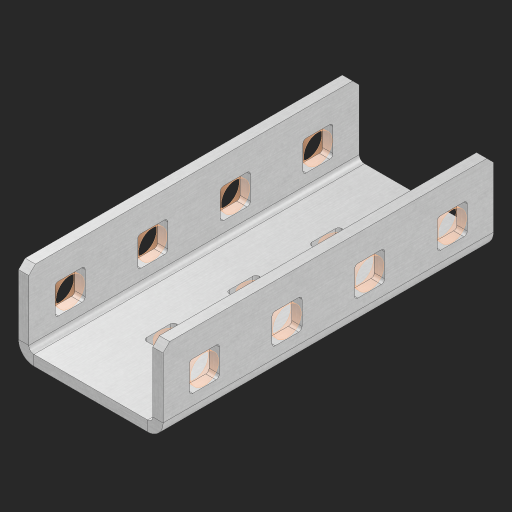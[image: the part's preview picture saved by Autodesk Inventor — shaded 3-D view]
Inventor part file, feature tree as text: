
AUTODESK INVENTOR PART (.ipt)
format: ipt  version: 2023 (Build 270158000, 158)  size: 441,856 bytes
history: native  units: in
note: dims shown in document units (in); Inventor stores cm internally (conversion verified against a paired STEP export)
features: other x17, extrude x9, sheet_metal_op x6, sketch x6, pattern_linear x1, chamfer x1
ambient origin geometry x8: Origin, YZ Plane, XZ Plane, XY Plane, X Axis, Y Axis, Z Axis, Center Point
bodies: Solid1 (feature_tree), Body (feature_tree)
feature tree (40):
  sheet_metal_op  "Flanges"
  other  "Flange Pattern Plane"
  other  "Flange Pattern Sketch"
  sheet_metal_op  "Flange Pattern"
  pattern_linear  "Center Pattern"  Spacing1=0.0625in  [1 undecoded]
  chamfer  "End Chamfer"
  sketch  "Sketch1"  dims[d0=0.875in]
  other  "Plate1"
  sketch  "Sketch2"  dims[d1=2.0in]
  other  "Plate2"
  sheet_metal_op  "Bend1"
  sheet_metal_op  "Corner1"
  sketch  "Sketch3"  dims[d2=0.0625in]
  sketch  "Sketch7"  dims[d3=0.0625in]
  other  "Srf1"
  other  "Srf2"
  sketch  "Sketch15"  dims[d4=0.0312in]
  sketch  "Sketch16"  dims[d5=0.125in d6=0.0625in d7=0.5in d8=90.0deg d9=0.0312in d10=0.25in d11=0.0625in d12=0.0625in d16=0.182in d17=0.02in d18=0.0625in d19=0.0in d20=0.25in d21=0.25in d38=1.5748in d40=0.5in d41=0.7874in d43=1.0in d46=0.172in d47=1.0in d48=0.0in d96=0.04in d97=0.25in d98=45.0deg d106=0.182in d107=0.02in d108=0.5in d110=0.0625in d111=0.0in d112=0.172in d113=0.5in d114=0.0in d117=0.5in d121=0.875in]
  other  "Srf786"
  other  "Srf823"
  other  "Srf824"
  other  "Srf825"
  other  "Srf826"
  other  "Srf827"
  other  "Srf828"
  other  "Srf889"
  other  "Srf890"
  sheet_metal_op  "Flange Stamp"
  sheet_metal_op  "Flange Circle"
  other  "Center Stamp"
  other  "Center Circle"
  extrude  "ExtrusionSrf2"  Depth=0.5in TaperAngle=90.0deg
  extrude  "ExtrusionSrf823"  Depth=0.25in
  extrude  "ExtrusionSrf824"  Depth=0.0625in
  extrude  "ExtrusionSrf825"  Depth=0.0625in
  extrude  "ExtrusionSrf826"  Depth=0.182in
  extrude  "ExtrusionSrf827"  Depth=0.02in
  extrude  "ExtrusionSrf828"  Depth=0.0625in
  extrude  "ExtrusionSrf889"  TaperAngle=0.0deg  [1 undecoded]
  extrude  "ExtrusionSrf890"  Depth=0.25in
note: 2 required parameter values undecoded (feature->parameter linkage not recoverable at this tier; creation-order binding heuristic only, values carry confidence <= 0.55)
